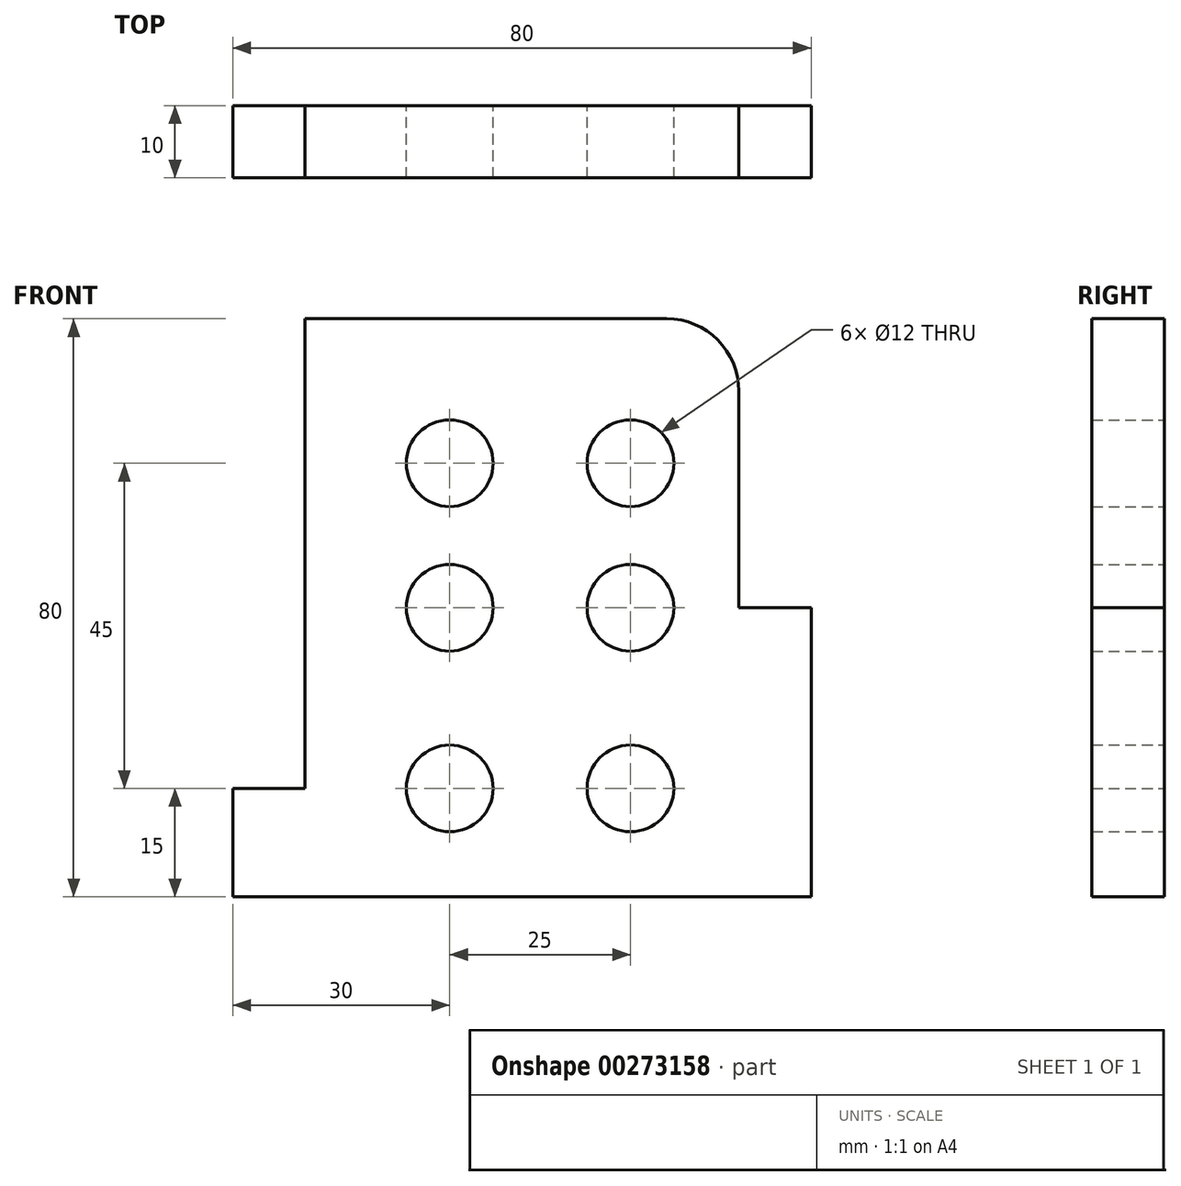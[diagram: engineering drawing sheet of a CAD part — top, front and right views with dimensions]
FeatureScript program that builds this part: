
annotation { "Feature Type Name" : "Feature", "Feature Type Description" : "" }
export const myFeature = defineFeature(function(context is Context, id is Id, definition is map)
    precondition{}
    {
        {
            var Q0;
            Q0=qCreatedBy(makeId("Front.planeOp"),FACE);
            var sketch = newSketch(context, id + "F0", { "sketchPlane" : qUnion([Q0])});
            skLineSegment(sketch, "E0", {"start": v(55, 15) * mm, "end": v(30, 15) * mm, "construction": true});
            skLineSegment(sketch, "E1", {"start": v(30, 60) * mm, "end": v(55, 60) * mm, "construction": true});
            skLineSegment(sketch, "E2", {"start": v(30, 40) * mm, "end": v(55, 40) * mm, "construction": true});
            skLineSegment(sketch, "E3", {"start": v(0, 0) * mm, "end": v(80, 0) * mm});
            skLineSegment(sketch, "E4", {"start": v(30, 60) * mm, "end": v(30, 40) * mm, "construction": true});
            skLineSegment(sketch, "E5", {"start": v(30, 40) * mm, "end": v(30, 15) * mm, "construction": true});
            skLineSegment(sketch, "E6", {"start": v(55, 60) * mm, "end": v(55, 40) * mm, "construction": true});
            skLineSegment(sketch, "E7", {"start": v(55, 40) * mm, "end": v(55, 15) * mm, "construction": true});
            skLineSegment(sketch, "E8", {"start": v(0, 0) * mm, "end": v(0, 15) * mm});
            skLineSegment(sketch, "E9", {"start": v(0, 15) * mm, "end": v(10, 15) * mm});
            skLineSegment(sketch, "E10", {"start": v(10, 15) * mm, "end": v(10, 80) * mm});
            skLineSegment(sketch, "E11", {"start": v(10, 80) * mm, "end": v(60, 80) * mm});
            skLineSegment(sketch, "E12", {"start": v(80, 0) * mm, "end": v(80, 40) * mm});
            skLineSegment(sketch, "E13", {"start": v(80, 40) * mm, "end": v(70, 40) * mm});
            skLineSegment(sketch, "E14", {"start": v(70, 40) * mm, "end": v(70, 70) * mm});
            skArc(sketch, "E15", {"start": v(60, 80) * mm, "mid": v(67.07, 77.07) * mm, "end": v(70, 70) * mm});
            skCircle(sketch, "E16", {"center": v(30, 60) * mm, "radius": 6 * mm});
            skCircle(sketch, "E17", {"center": v(55, 60) * mm, "radius": 6 * mm});
            skCircle(sketch, "E18", {"center": v(30, 40) * mm, "radius": 6 * mm});
            skCircle(sketch, "E19", {"center": v(55, 40) * mm, "radius": 6 * mm});
            skCircle(sketch, "E20", {"center": v(30, 15) * mm, "radius": 6 * mm});
            skCircle(sketch, "E21", {"center": v(55, 15) * mm, "radius": 6 * mm});
            skSolve(sketch);
        }
        {
            var Q0;
            Q0=makeQuery(id+"F0.imprint","IMPRINT",FACE,{"disambiguationData":[TD([[makeQuery(id+"F0.imprint","IMPRINT",EDGE,{"derivedFrom":sQuery(id+"F0.wireOp",EDGE,"E3")}),1.0]])]});
            extrude(context, id + "F1", {"entities" : qUnion([Q0]), "depth" : 10 * mm});
        }
    });
